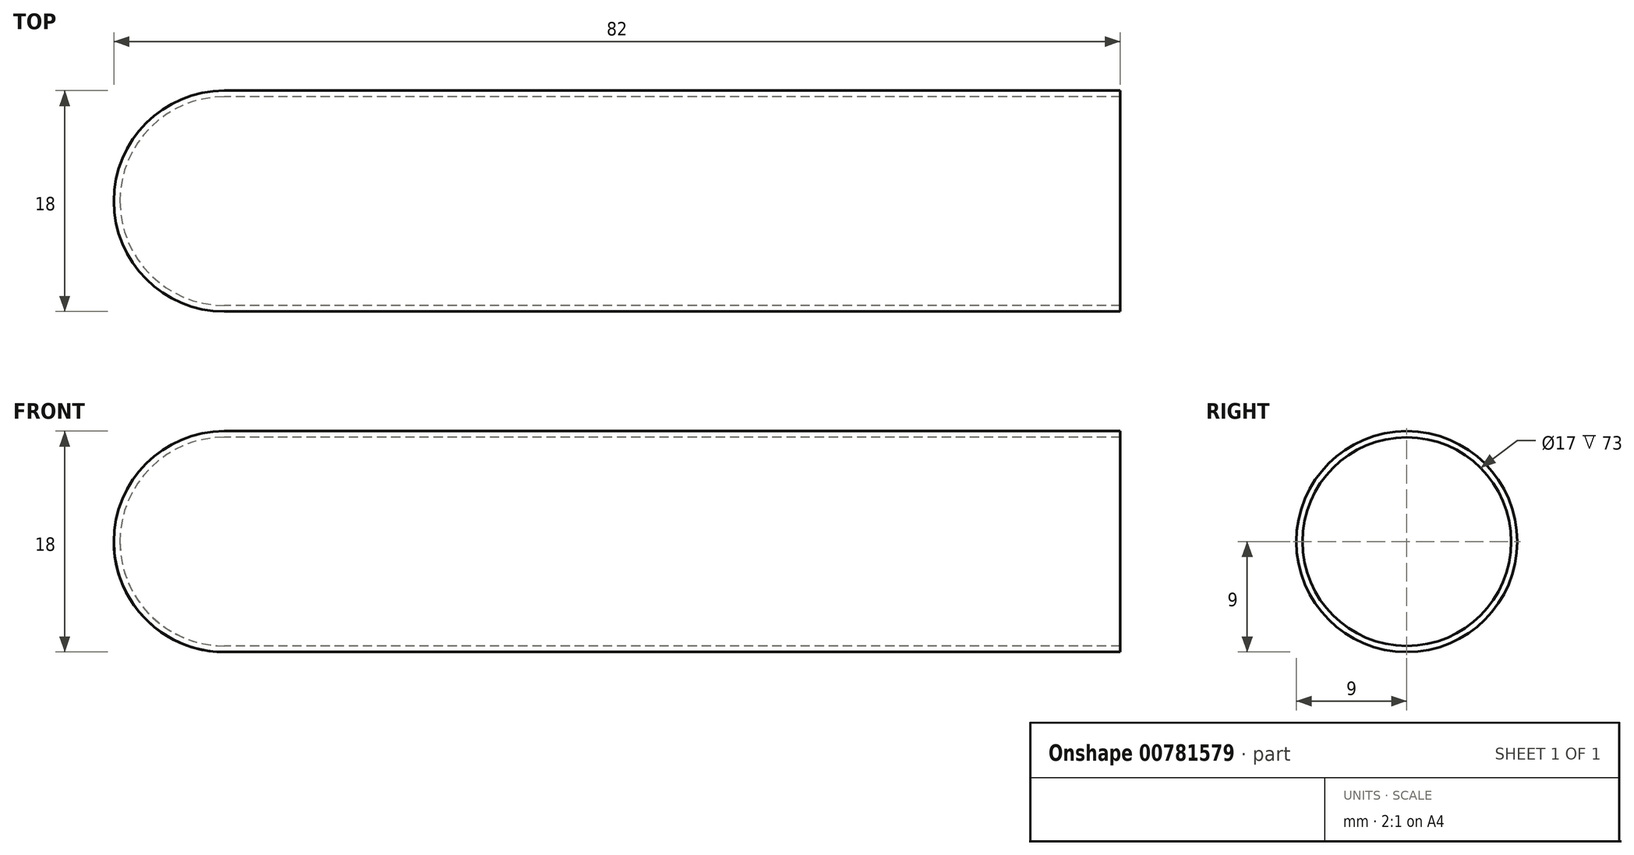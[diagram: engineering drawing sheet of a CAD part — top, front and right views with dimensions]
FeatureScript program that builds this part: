
annotation { "Feature Type Name" : "Feature", "Feature Type Description" : "" }
export const myFeature = defineFeature(function(context is Context, id is Id, definition is map)
    precondition{}
    {
        {
            var Q0;
            Q0=qCreatedBy(makeId("Right.planeOp"),FACE);
            var sketch = newSketch(context, id + "F0", { "sketchPlane" : qUnion([Q0])});
            skCircle(sketch, "E0", {"center": v(0, 0) * mm, "radius": 9 * mm});
            skSolve(sketch);
        }
        {
            var Q0;
            Q0 = qSketchRegion(id + "F0", true);
            extrude(context, id + "F1", {"entities" : qUnion([Q0]), "depth" : (73 + 9) * mm, "offsetDistance" : 25 * mm, "symmetric" : true});
        }
        {
            var Q0;
            Q0=makeQuery(id+"F1.opExtrude","CAP_EDGE",EDGE,{"disambiguationData":[OSD([sQuery(id+"F0.wireOp",EDGE,"E0")])],"isStart":true});
            fillet(context, id + "F2", {"entities" : qUnion([Q0]), "radius" : 9 * mm, "tangentPropagation" : true, "allowEdgeOverflow" : false});
        }
        {
            var Q0;
            Q0=makeQuery(id+"F1.opExtrude","CAP_FACE",FACE,{"disambiguationData":[OSD([sQuery(id+"F0.wireOp",EDGE,"E0")])],"isStart":false});
            shell(context, id + "F3", {"entities" : qUnion([Q0]), "thickness" : .5 * mm});
        }
    });
